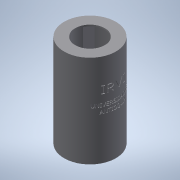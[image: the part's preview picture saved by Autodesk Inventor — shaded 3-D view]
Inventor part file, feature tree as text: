
AUTODESK INVENTOR PART (.ipt)
format: ipt  version: 2021.3 (Build 253353010, 353A)  size: 1,086,464 bytes
history: native  units: mm
features: sketch x8, extrude x6, emboss x3, plane x2, mirror x1
ambient origin geometry x8: Origin, YZ Plane, XZ Plane, XY Plane, X Axis, Y Axis, Z Axis, Center Point
bodies: Solid1 (feature_tree)
feature tree (20):
  extrude  "Extrusion1"  Depth=125.0mm TaperAngle=0.0deg
  extrude  "Extrusion2"  Depth=123.0mm TaperAngle=0.0deg
  plane  "Work Plane1"
  plane  "Work Plane2"
  extrude  "Extrusion3"  Depth=43.046mm
  mirror  "Mirror1"
  extrude  "Extrusion4"  Depth=40.0mm
  emboss  "Emboss1"
  sketch  "Sketch7"  dims[d29=12.0mm d30=0.0mm d31=2.0mm d32=0.0mm]
  emboss  "Emboss2"
  emboss  "Emboss3"
  extrude  "Extrusion7"  Depth=2.0mm TaperAngle=0.0deg
  extrude  "Extrusion8"  Depth=2.0mm TaperAngle=0.0deg
  sketch  "Sketch1"  dims[d0=70.0mm d1=125.0mm d2=0.0mm]
  sketch  "Sketch2"  dims[d3=67.0mm d4=123.0mm d5=0.0mm]
  sketch  "Sketch3"  dims[d6=20.0mm d7=-20.0mm d8=43.046mm]
  sketch  "Sketch4"  dims[d9=2.0mm d10=0.0mm d11=40.0mm]
  sketch  "Sketch6"  dims[d12=0.0mm d13=0.0mm d27=2.0mm d28=0.0mm]
  sketch  "Sketch9"  dims[d35=2.727mm]
  sketch  "Sketch10"  dims[d37=2.727mm d38=0.0mm d39=0.0mm d40=2.727mm d41=2.727mm d42=2.727mm d43=0.0mm d44=0.0mm]
